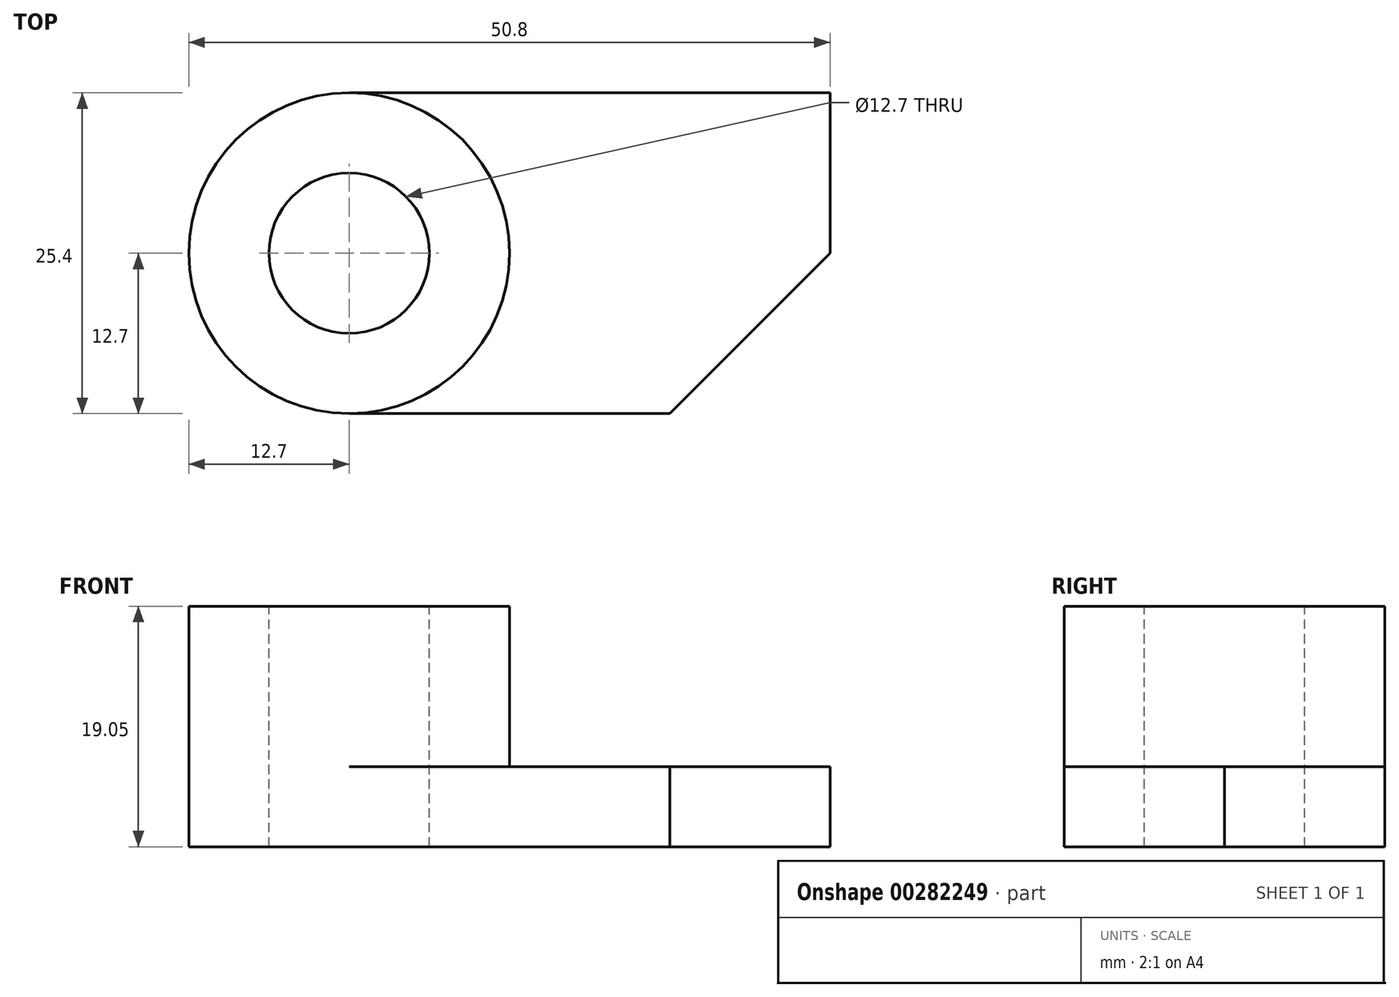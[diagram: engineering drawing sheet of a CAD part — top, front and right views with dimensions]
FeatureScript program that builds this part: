
annotation { "Feature Type Name" : "Feature", "Feature Type Description" : "" }
export const myFeature = defineFeature(function(context is Context, id is Id, definition is map)
    precondition{}
    {
        {
            var Q0;
            Q0=qCreatedBy(makeId("Top.planeOp"),FACE);
            var sketch = newSketch(context, id + "F0", { "sketchPlane" : qUnion([Q0])});
            skLineSegment(sketch, "E0.bottom", {"start": v(0, 0) * mm, "end": v(38.1, 0) * mm});
            skLineSegment(sketch, "E0.top", {"start": v(0, 25.4) * mm, "end": v(38.1, 25.4) * mm});
            skLineSegment(sketch, "E0.left", {"start": v(0, 0) * mm, "end": v(0, 25.4) * mm});
            skLineSegment(sketch, "E0.right", {"start": v(38.1, 0) * mm, "end": v(38.1, 25.4) * mm});
            skSolve(sketch);
        }
        {
            var Q0;
            Q0 = qSketchRegion(id + "F0", true);
            extrude(context, id + "F1", {"entities" : qUnion([Q0]), "depth" : 6.35 * mm});
        }
        {
            var Q0;
            Q0=qCreatedBy(makeId("Top.planeOp"),FACE);
            var sketch = newSketch(context, id + "F2", { "sketchPlane" : qUnion([Q0])});
            skCircle(sketch, "E1", {"center": v(0, 12.7) * mm, "radius": 12.7 * mm});
            skSolve(sketch);
        }
        {
            var Q0;
            Q0 = qSketchRegion(id + "F2", true);
            extrude(context, id + "F3", {"entities" : qUnion([Q0]), "operationType" : NewBodyOperationType.ADD, "depth" : 19.05 * mm});
        }
        {
            var Q0;
            Q0=makeQuery(id+"F3.opExtrude","CAP_FACE",FACE,{"disambiguationData":[OSD([sQuery(id+"F2.wireOp",EDGE,"E1")])],"isStart":false});
            var sketch = newSketch(context, id + "F4", { "sketchPlane" : qUnion([Q0])});
            skCircle(sketch, "E2", {"center": v(0, 12.7) * mm, "radius": 6.35 * mm});
            skSolve(sketch);
        }
        {
            var Q0;
            Q0 = qSketchRegion(id + "F4", true);
            extrude(context, id + "F5", {"entities" : qUnion([Q0]), "operationType" : NewBodyOperationType.REMOVE, "oppositeDirection" : true, "depth" : 19.05 * mm});
        }
        {
            var Q0;
            Q0=qCreatedBy(makeId("Top.planeOp"),FACE);
            var sketch = newSketch(context, id + "F6", { "sketchPlane" : qUnion([Q0])});
            skLineSegment(sketch, "E3", {"start": v(25.4, 0) * mm, "end": v(38.1, 0) * mm});
            skLineSegment(sketch, "E4", {"start": v(38.1, 0) * mm, "end": v(38.1, 12.7) * mm});
            skLineSegment(sketch, "E5", {"start": v(38.1, 12.7) * mm, "end": v(25.4, 0) * mm});
            skSolve(sketch);
        }
        {
            var Q0;
            Q0 = qSketchRegion(id + "F6", true);
            extrude(context, id + "F7", {"entities" : qUnion([Q0]), "operationType" : NewBodyOperationType.REMOVE, "depth" : 6.35 * mm});
        }
    });
